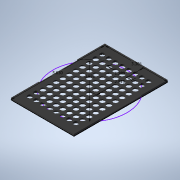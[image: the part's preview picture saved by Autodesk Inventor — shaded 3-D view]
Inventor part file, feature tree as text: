
AUTODESK INVENTOR PART (.ipt)
format: ipt  version: 2020 (Build 240168000, 168)  size: 333,312 bytes
history: native  units: in
note: dims shown in document units (in); Inventor stores cm internally (conversion verified against a paired STEP export)
features: sketch x2, extrude x2, hole x1, pattern_linear x1
ambient origin geometry x8: Origin, YZ Plane, XZ Plane, XY Plane, X Axis, Y Axis, Z Axis, Center Point
bodies: Solid1 (feature_tree)
feature tree (6):
  sketch  "Sketch1"  dims[d0=3.3654in d1=5.0299in]
  extrude  "Extrusion1"  Depth=5.0299in
  extrude  "Extrusion2"  Depth=0.0625in
  hole  "Hole1"  [1 undecoded]
  pattern_linear  "Rectangular Pattern1"  Spacing1=0.1019in  [1 undecoded]
  sketch  "Sketch2"  dims[d2=2.515in d3=3.9764in d4=1.2795in d5=0.1019in d6=0.0in d7=0.0625in d8=0.0in d9=0.2362in d10=0.0in d11=0.2756in d12=0.75in d13=0.438in d14=0.25in d15=0.5635in d16=1.0in d17=0.8108in d18=4.7244in d20=0.3543in d21=3.1496in d23=0.3543in d24=0.2362in d25=0.2362in d26=0.5661in d27=0.4465in]
note: 2 required parameter values undecoded (feature->parameter linkage not recoverable at this tier; creation-order binding heuristic only, values carry confidence <= 0.55)
